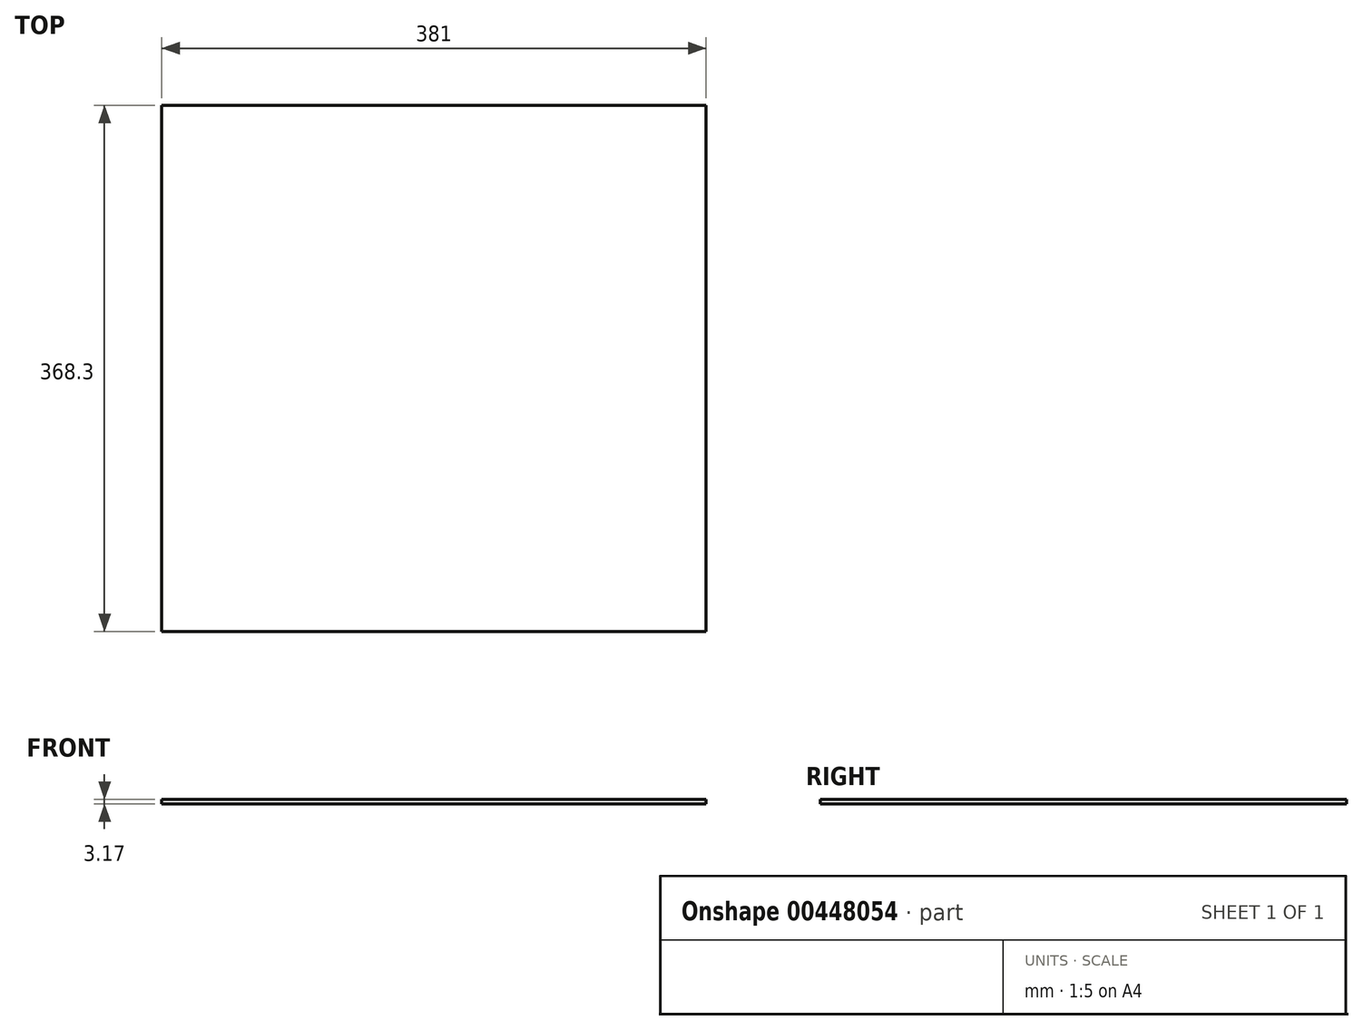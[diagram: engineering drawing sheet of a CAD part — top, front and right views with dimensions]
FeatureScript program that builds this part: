
annotation { "Feature Type Name" : "Feature", "Feature Type Description" : "" }
export const myFeature = defineFeature(function(context is Context, id is Id, definition is map)
    precondition{}
    {
        {
            var Q0;
            Q0=qCreatedBy(makeId("Top.planeOp"),FACE);
            var sketch = newSketch(context, id + "F0", { "sketchPlane" : qUnion([Q0])});
            skLineSegment(sketch, "E0.bottom", {"start": v(-190.5, 184.15) * mm, "end": v(190.5, 184.15) * mm});
            skLineSegment(sketch, "E0.top", {"start": v(-190.5, -184.15) * mm, "end": v(190.5, -184.15) * mm});
            skLineSegment(sketch, "E0.left", {"start": v(-190.5, 184.15) * mm, "end": v(-190.5, -184.15) * mm});
            skLineSegment(sketch, "E0.right", {"start": v(190.5, 184.15) * mm, "end": v(190.5, -184.15) * mm});
            skPoint(sketch, "E0.middle", {"position": v(0, 0) * mm});
            skSolve(sketch);
        }
        {
            var Q0;
            Q0 = qSketchRegion(id + "F0", true);
            extrude(context, id + "F1", {"entities" : qUnion([Q0]), "depth" : 3.17 * mm});
        }
    });
